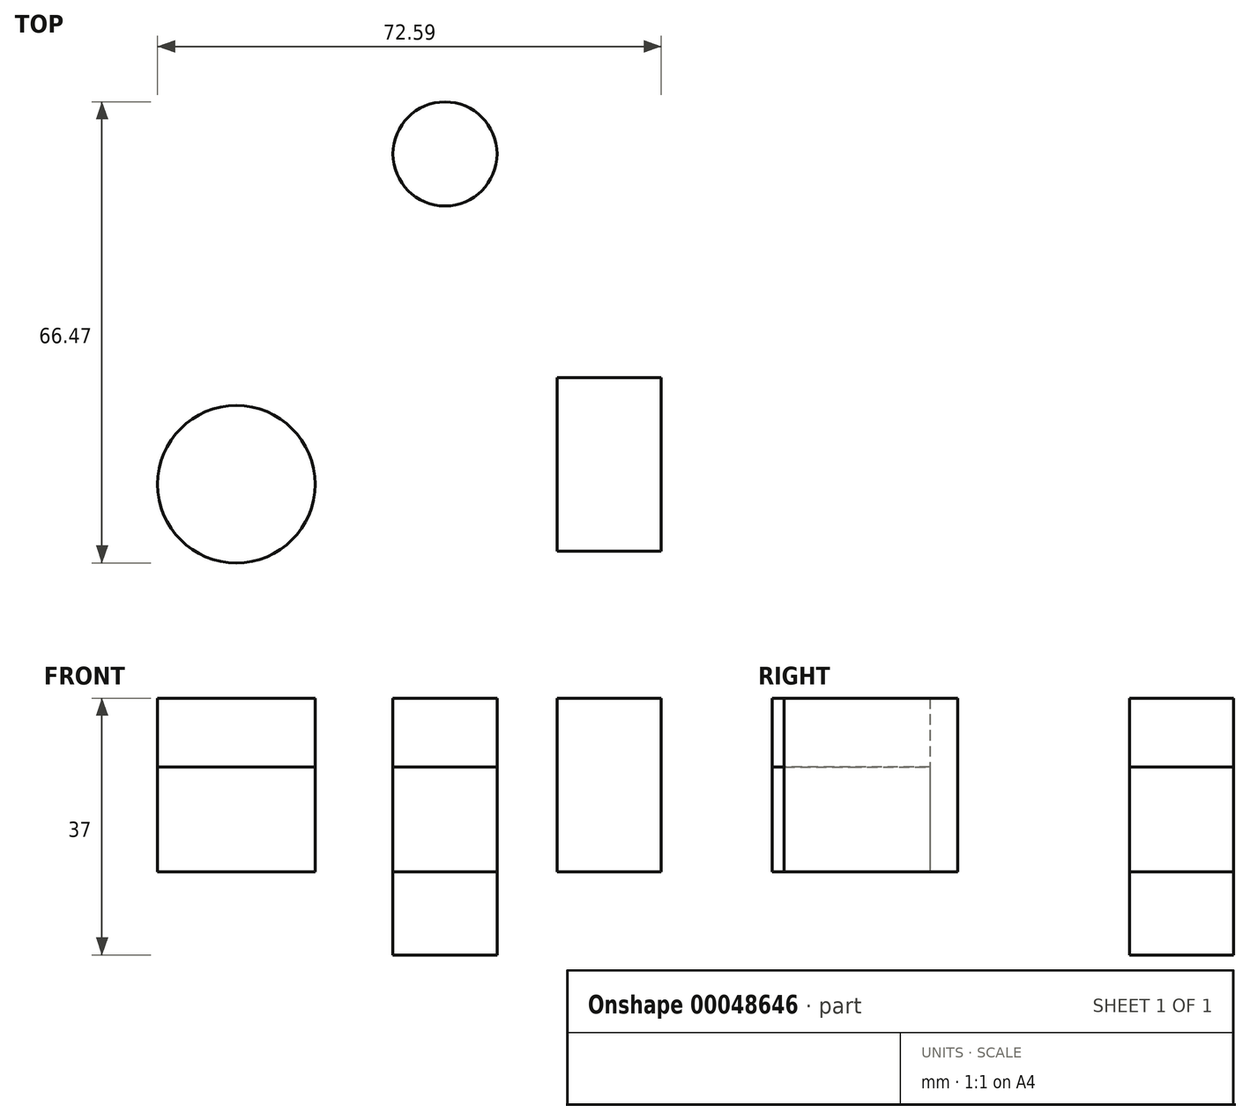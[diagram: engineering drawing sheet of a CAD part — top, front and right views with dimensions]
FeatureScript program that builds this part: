
annotation { "Feature Type Name" : "Feature", "Feature Type Description" : "" }
export const myFeature = defineFeature(function(context is Context, id is Id, definition is map)
    precondition{}
    {
        {
            var Q0;
            Q0=qCreatedBy(makeId("Top.planeOp"),FACE);
            var sketch = newSketch(context, id + "F0", { "sketchPlane" : qUnion([Q0])});
            skLineSegment(sketch, "E0", {"start": v(-9.46, -16.1) * mm, "end": v(-9.46, -24.33) * mm});
            skLineSegment(sketch, "E1", {"start": v(-9.2, -24.33) * mm, "end": v(-2.79, -24.33) * mm});
            skLineSegment(sketch, "E2", {"start": v(2.54, -16.1) * mm, "end": v(-9.46, -16.1) * mm});
            skLineSegment(sketch, "E3", {"start": v(29.91, -15.04) * mm, "end": v(29.91, -40.04) * mm});
            skLineSegment(sketch, "E4", {"start": v(29.91, -40.04) * mm, "end": v(44.91, -40.04) * mm});
            skLineSegment(sketch, "E5", {"start": v(44.91, -40.04) * mm, "end": v(44.91, -15.04) * mm});
            skLineSegment(sketch, "E6", {"start": v(44.91, -15.04) * mm, "end": v(29.91, -15.04) * mm});
            skLineSegment(sketch, "E7", {"start": v(-55.48, -24.06) * mm, "end": v(-55.48, -38.04) * mm});
            skLineSegment(sketch, "E8", {"start": v(-55.48, -38.04) * mm, "end": v(-19.15, -38.04) * mm});
            skLineSegment(sketch, "E9", {"start": v(-19.15, -38.04) * mm, "end": v(-19.15, -28.55) * mm});
            skLineSegment(sketch, "E10", {"start": v(-19.65, -28.43) * mm, "end": v(-23.64, -28.55) * mm});
            skLineSegment(sketch, "E11", {"start": v(-23.64, -28.55) * mm, "end": v(-23.48, -33.66) * mm});
            skLineSegment(sketch, "E12", {"start": v(-23.9, -33.55) * mm, "end": v(-35.88, -33.55) * mm});
            skLineSegment(sketch, "E13", {"start": v(-36.13, -32.8) * mm, "end": v(-36.13, -25.18) * mm});
            skLineSegment(sketch, "E14", {"start": v(-35.75, -25.18) * mm, "end": v(-43.37, -25.18) * mm});
            skLineSegment(sketch, "E15", {"start": v(-43.37, -25.3) * mm, "end": v(-43.37, -33.8) * mm});
            skLineSegment(sketch, "E16", {"start": v(-43.37, -33.55) * mm, "end": v(-52.6, -33.55) * mm});
            skLineSegment(sketch, "E17", {"start": v(-52.73, -33.05) * mm, "end": v(-52.73, -23.93) * mm});
            skLineSegment(sketch, "E18", {"start": v(-53.1, -23.68) * mm, "end": v(-55.48, -24.06) * mm});
            skSolve(sketch);
        }
        {
            var Q0;
            Q0=sQuery(id+"F0.wireOp",EDGE,"E3");
            var Q1;
            Q1=sQuery(id+"F0.wireOp",EDGE,"E4");
            var Q2;
            Q2=sQuery(id+"F0.wireOp",EDGE,"E5");
            var Q3;
            Q3=sQuery(id+"F0.wireOp",EDGE,"E6");
            var Q4;
            Q4=sQuery(id+"F0.wireOp",EDGE,"E17");
            extrude(context, id + "F1", {"bodyType" : ToolBodyType.SURFACE, "surfaceEntities" : qUnion([Q0, Q1, Q2, Q3, Q4]), "depth" : 69.13 * mm});
        }
        {
            var Q0;
            Q0=qCreatedBy(makeId("Top.planeOp"),FACE);
            var sketch = newSketch(context, id + "F2", { "sketchPlane" : qUnion([Q0])});
            skCircle(sketch, "E19", {"center": v(13.74, 17.22) * mm, "radius": 7.5 * mm});
            skCircle(sketch, "E20", {"center": v(-16.33, -30.4) * mm, "radius": 11.35 * mm});
            skSolve(sketch);
        }
        {
            var Q0;
            Q0 = qSketchRegion(id + "F0", true);
            extrude(context, id + "F3", {"entities" : qUnion([Q0]), "depth" : 25 * mm});
        }
        {
            var Q0;
            Q0 = qSketchRegion(id + "F2", true);
            extrude(context, id + "F4", {"entities" : qUnion([Q0]), "depth" : 25 * mm});
        }
        {
            var Q0;
            Q0=makeQuery(id+"F4.opExtrude","CAP_FACE",FACE,{"disambiguationData":[OSD([sQuery(id+"F2.wireOp",EDGE,"E20")])],"isStart":false});
            var Q1;
            Q1=makeQuery(id+"F4.opExtrude","CAP_FACE",FACE,{"disambiguationData":[OSD([sQuery(id+"F2.wireOp",EDGE,"E19")])],"isStart":false});
            var Q2;
            Q2=makeQuery(id+"F4.opExtrude","CAP_FACE",FACE,{"disambiguationData":[OSD([sQuery(id+"F2.wireOp",EDGE,"E19")])],"isStart":true});
            extrude(context, id + "F5", {"entities" : qUnion([Q0, Q1, Q2]), "operationType" : NewBodyOperationType.ADD, "oppositeDirection" : true, "depth" : 12 * mm});
        }
        {
            var Q0;
            Q0 = qSketchRegion(id + "F2", true);
            extrude(context, id + "F6", {"entities" : qUnion([Q0]), "depth" : 15.07 * mm});
        }
    });
